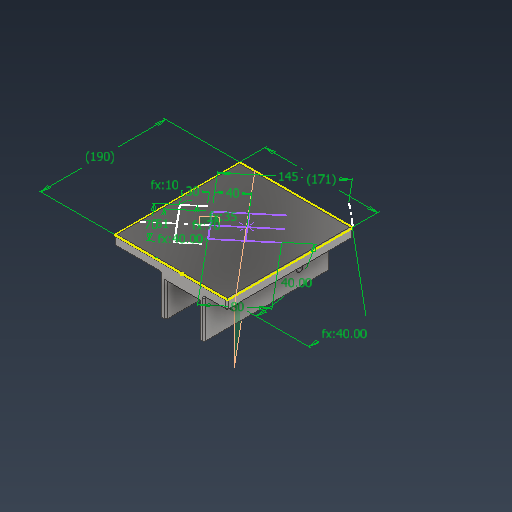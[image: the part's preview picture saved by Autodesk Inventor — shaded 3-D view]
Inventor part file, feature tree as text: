
AUTODESK INVENTOR PART (.ipt)
format: ipt  version: 2021 (Build 250183000, 183)  size: 244,736 bytes
history: native  units: mm
features: sketch x4, extrude x3, other x2, plane x2, hole x1, fillet x1, chamfer x1
ambient origin geometry x8: Origin, YZ Plane, XZ Plane, XY Plane, X Axis, Y Axis, Z Axis, Center Point
bodies: Solid1 (feature_tree)
feature tree (14):
  extrude  "clamp_base"  Depth=66.0mm
  extrude  "clamp_extrusion"  TaperAngle=0.0deg  [1 undecoded]
  extrude  "platform"  Depth=50.0mm
  hole  "clampHole"  [1 undecoded]
  other  "tabWeld"
  plane  "Work Plane4"
  other  "reelWeld"
  fillet  "Fillet1"  [1 undecoded]
  chamfer  "Chamfer1"  Distance=1149.0mm
  plane  "Work Plane5"
  sketch  "Sketch1"  dims[d0=58.0mm d1=66.0mm]
  sketch  "Sketch2"  dims[d2=33.0mm d3=0.0mm]
  sketch  "Sketch4"  dims[d4=190.0mm d5=0.0mm d6=50.0mm]
  sketch  "Sketch8"  dims[d7=50.0mm d8=25.0mm d9=0.0mm d10=0.0mm d12=1149.0mm d13=15.0mm d14=0.0mm d15=51.0mm d35=0.0mm d36=0.0mm d37=70.0mm d38=35.0mm d51=45.0mm d53=10.0mm d54=6.0mm d55=4.0mm d56=2.0mm d57=90.0deg d58=8.0mm d59=20.594885mm d60=100.0mm d61=190.0mm d63=80.0mm d64=51.0mm d67=6.981317mm d68=171.0mm d70=40.0mm d71=190.0mm d73=90.0deg d74=10.0mm d75=6.981317mm d77=30.0mm d78=70.0mm d79=70.0mm d81=2.0mm d82=2.0mm d83=2.0mm d84=45.0deg d86=35.0mm d87=10.0mm d88=6.981317mm d89=145.0mm]
note: 3 required parameter values undecoded (feature->parameter linkage not recoverable at this tier; creation-order binding heuristic only, values carry confidence <= 0.55)
